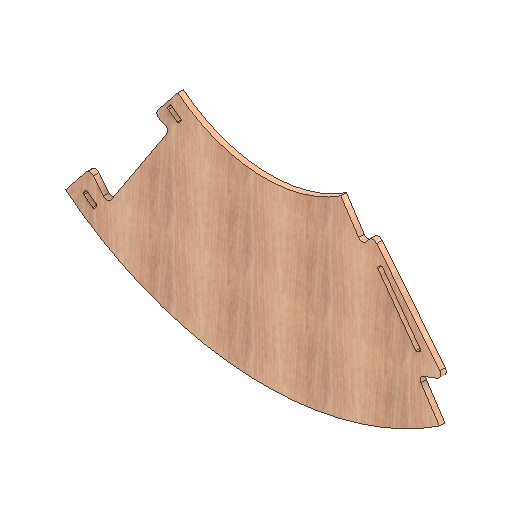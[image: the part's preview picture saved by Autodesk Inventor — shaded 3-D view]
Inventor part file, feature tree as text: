
AUTODESK INVENTOR PART (.ipt)
format: ipt  version: 2021 (Build 250183000, 183)  size: 279,040 bytes
history: native  units: mm
features: other x2, extrude x2, hole x1
ambient origin geometry x8: Origin, YZ Plane, XZ Plane, XY Plane, X Axis, Y Axis, Z Axis, Center Point
bodies: Solid1 (feature_tree)
feature tree (5):
  other  "CONTOURS"
  hole  "HOLES"  [1 undecoded]
  other  "LETTERS"
  extrude  "Extrusion1"  Depth=18.0mm TaperAngle=0.0deg
  extrude  "Extrusion2"  [1 undecoded]
note: 2 required parameter values undecoded (feature->parameter linkage not recoverable at this tier; creation-order binding heuristic only, values carry confidence <= 0.55)
